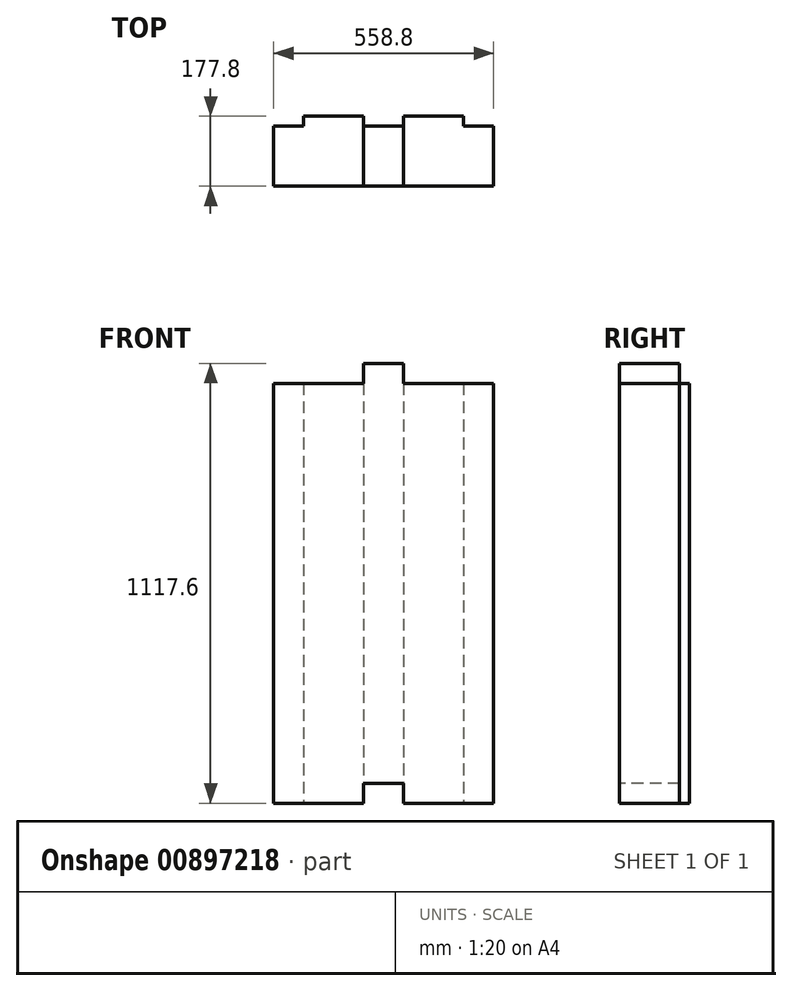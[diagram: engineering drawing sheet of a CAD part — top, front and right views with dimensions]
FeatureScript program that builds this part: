
annotation { "Feature Type Name" : "Feature", "Feature Type Description" : "" }
export const myFeature = defineFeature(function(context is Context, id is Id, definition is map)
    precondition{}
    {
        {
            var Q0;
            Q0=qCreatedBy(makeId("Top.planeOp"),FACE);
            var sketch = newSketch(context, id + "F0", { "sketchPlane" : qUnion([Q0])});
            skLineSegment(sketch, "E0", {"start": v(0, 0) * mm, "end": v(76.2, 0) * mm});
            skLineSegment(sketch, "E1", {"start": v(76.2, 0) * mm, "end": v(76.2, 25.4) * mm});
            skLineSegment(sketch, "E2", {"start": v(76.2, 25.4) * mm, "end": v(228.6, 25.4) * mm});
            skLineSegment(sketch, "E3", {"start": v(228.6, 25.4) * mm, "end": v(228.6, 0) * mm});
            skLineSegment(sketch, "E4", {"start": v(228.6, 0) * mm, "end": v(330.2, 0) * mm});
            skLineSegment(sketch, "E5", {"start": v(330.2, 0) * mm, "end": v(330.2, 25.4) * mm});
            skLineSegment(sketch, "E6", {"start": v(330.2, 25.4) * mm, "end": v(482.6, 25.4) * mm});
            skLineSegment(sketch, "E7", {"start": v(482.6, 25.4) * mm, "end": v(482.6, 0) * mm});
            skLineSegment(sketch, "E8", {"start": v(482.6, 0) * mm, "end": v(558.8, 0) * mm});
            skLineSegment(sketch, "E9", {"start": v(558.8, 0) * mm, "end": v(558.8, -152.4) * mm});
            skLineSegment(sketch, "E10", {"start": v(558.8, -152.4) * mm, "end": v(0, -152.4) * mm});
            skLineSegment(sketch, "E11", {"start": v(0, -152.4) * mm, "end": v(0, 0) * mm});
            skSolve(sketch);
        }
        {
            var Q0;
            Q0 = qSketchRegion(id + "F0", true);
            extrude(context, id + "F1", {"entities" : qUnion([Q0]), "depth" : 1066.8 * mm, "offsetDistance" : 25.4 * mm});
        }
        {
            var Q0;
            Q0=makeQuery(id+"F1.opExtrude","SWEPT_FACE",FACE,{"disambiguationData":[OSD([sQuery(id+"F0.wireOp",EDGE,"E10")])]});
            cPlane(context, id + "F2", {"entities" : qUnion([Q0]), "cplaneType" : CPlaneType.OFFSET, "offset" : 0 * mm, "width" : 152.4 * mm, "height" : 152.4 * mm});
        }
        {
            var Q0;
            Q0=qCreatedBy(id+"F2.planeOp",FACE);
            var sketch = newSketch(context, id + "F3", { "sketchPlane" : qUnion([Q0])});
            skLineSegment(sketch, "E12.bottom", {"start": v(330.2, 1066.8) * mm, "end": v(228.6, 1066.8) * mm});
            skLineSegment(sketch, "E12.top", {"start": v(330.2, 1117.6) * mm, "end": v(228.6, 1117.6) * mm});
            skLineSegment(sketch, "E12.left", {"start": v(330.2, 1066.8) * mm, "end": v(330.2, 1117.6) * mm});
            skLineSegment(sketch, "E12.right", {"start": v(228.6, 1066.8) * mm, "end": v(228.6, 1117.6) * mm});
            skSolve(sketch);
        }
        {
            var Q0;
            Q0 = qSketchRegion(id + "F3", true);
            extrude(context, id + "F4", {"entities" : qUnion([Q0]), "operationType" : NewBodyOperationType.ADD, "oppositeDirection" : true, "depth" : 152.4 * mm, "offsetDistance" : 25.4 * mm});
        }
        {
            var Q0;
            Q0=qCreatedBy(id+"F2.planeOp",FACE);
            var sketch = newSketch(context, id + "F5", { "sketchPlane" : qUnion([Q0])});
            skLineSegment(sketch, "E13.bottom", {"start": v(330.2, 0) * mm, "end": v(228.6, 0) * mm});
            skLineSegment(sketch, "E13.top", {"start": v(330.2, 50.8) * mm, "end": v(228.6, 50.8) * mm});
            skLineSegment(sketch, "E13.left", {"start": v(330.2, 0) * mm, "end": v(330.2, 50.8) * mm});
            skLineSegment(sketch, "E13.right", {"start": v(228.6, 0) * mm, "end": v(228.6, 50.8) * mm});
            skSolve(sketch);
        }
        {
            var Q0;
            Q0 = qSketchRegion(id + "F5", true);
            extrude(context, id + "F6", {"entities" : qUnion([Q0]), "operationType" : NewBodyOperationType.REMOVE, "endBound" : BoundingType.THROUGH_ALL, "oppositeDirection" : true, "depth" : 25.4 * mm, "offsetDistance" : 25.4 * mm});
        }
    });
